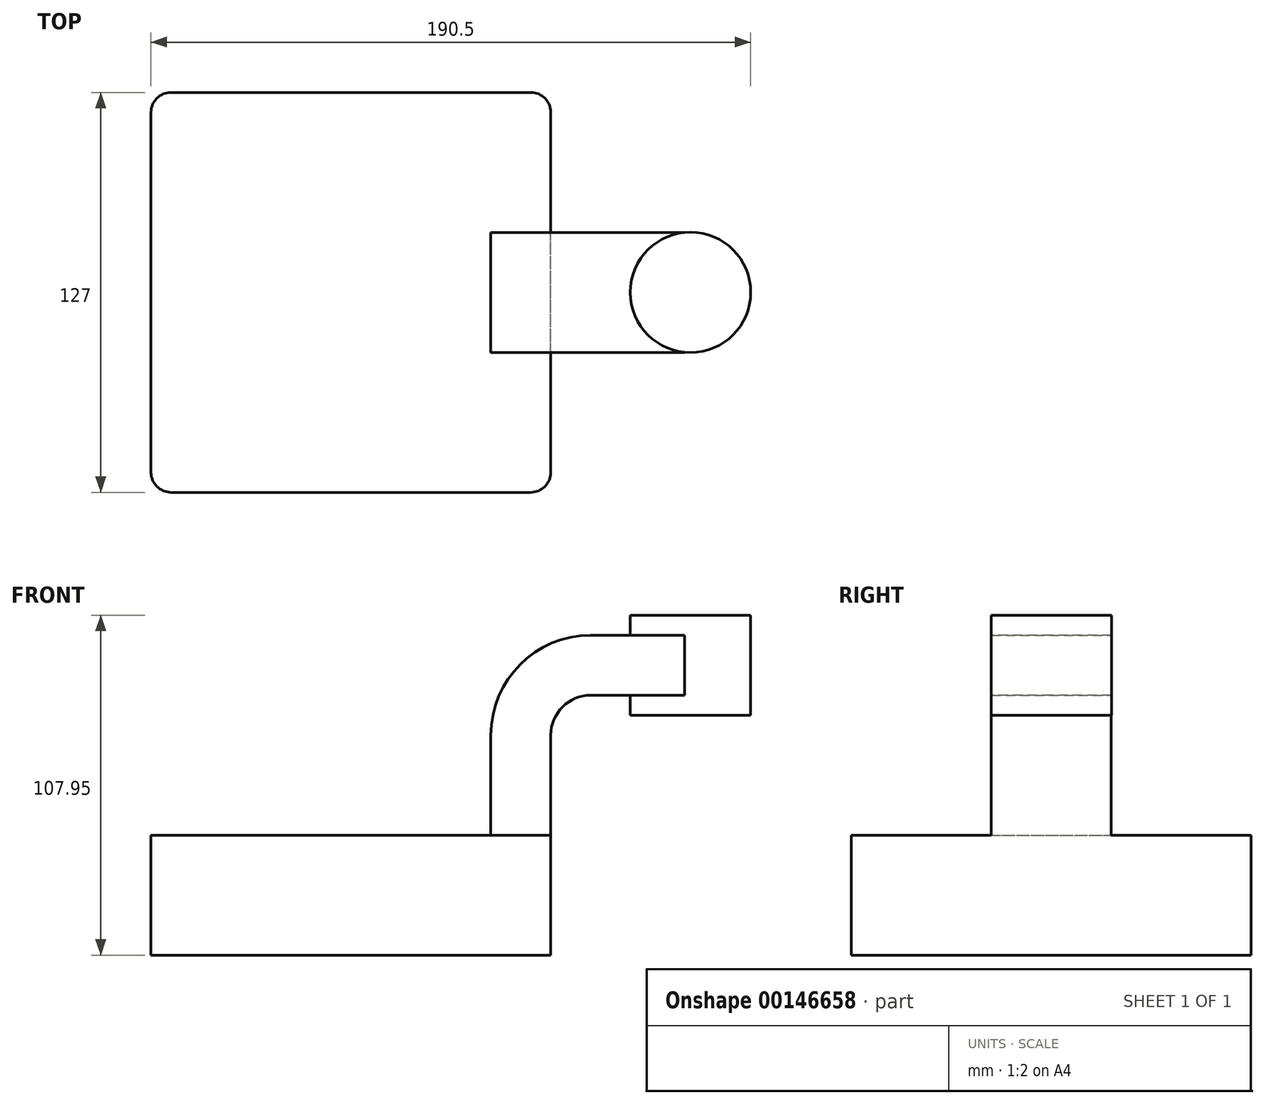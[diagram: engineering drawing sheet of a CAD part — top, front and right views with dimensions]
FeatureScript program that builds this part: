
annotation { "Feature Type Name" : "Feature", "Feature Type Description" : "" }
export const myFeature = defineFeature(function(context is Context, id is Id, definition is map)
    precondition{}
    {
        {
            var Q0;
            Q0=qCreatedBy(makeId("Front.planeOp"),FACE);
            var sketch = newSketch(context, id + "F0", { "sketchPlane" : qUnion([Q0])});
            skLineSegment(sketch, "E0.bottom", {"start": v(63.5, 19.05) * mm, "end": v(-63.5, 19.05) * mm});
            skLineSegment(sketch, "E0.top", {"start": v(63.5, -19.05) * mm, "end": v(-63.5, -19.05) * mm});
            skLineSegment(sketch, "E0.left", {"start": v(63.5, 19.05) * mm, "end": v(63.5, -19.05) * mm});
            skLineSegment(sketch, "E0.right", {"start": v(-63.5, 19.05) * mm, "end": v(-63.5, -19.05) * mm});
            skPoint(sketch, "E0.middle", {"position": v(0, 0) * mm});
            skLineSegment(sketch, "E1.bottom", {"start": v(127, 57.15) * mm, "end": v(88.9, 57.15) * mm});
            skLineSegment(sketch, "E1.top", {"start": v(127, 88.9) * mm, "end": v(88.9, 88.9) * mm});
            skLineSegment(sketch, "E1.left", {"start": v(127, 57.15) * mm, "end": v(127, 88.9) * mm});
            skLineSegment(sketch, "E1.right", {"start": v(88.9, 57.15) * mm, "end": v(88.9, 88.9) * mm});
            skPoint(sketch, "E1.middle", {"position": v(107.95, 73.03) * mm});
            skLineSegment(sketch, "E2", {"start": v(63.5, 19.05) * mm, "end": v(63.5, 50.8) * mm});
            skArc(sketch, "E3", {"start": v(63.5, 50.8) * mm, "mid": v(67.22, 59.78) * mm, "end": v(76.2, 63.5) * mm});
            skLineSegment(sketch, "E4", {"start": v(76.2, 63.5) * mm, "end": v(107.86, 63.5) * mm});
            skLineSegment(sketch, "E5.0", {"start": v(76.2, 82.55) * mm, "end": v(107.86, 82.55) * mm});
            skArc(sketch, "E5.1", {"start": v(44.45, 50.8) * mm, "mid": v(53.75, 73.25) * mm, "end": v(76.2, 82.55) * mm});
            skLineSegment(sketch, "E5.2", {"start": v(44.45, 19.05) * mm, "end": v(44.45, 50.8) * mm});
            skLineSegment(sketch, "E6", {"start": v(107.86, 57.15) * mm, "end": v(107.86, 88.9) * mm});
            skFitSpline(sketch, "E7", {"points": [v(-63.5, 19.05) * mm, v(76.2, 82.55) * mm], "startDerivative": vector(59.97, 153.39) * mm, "endDerivative": vector(184.43, -1.79) * mm});
            skSolve(sketch);
        }
        {
            var Q0;
            Q0=makeQuery(id+"F0.imprint","IMPRINT",FACE,{"disambiguationData":[TD([[makeQuery(id+"F0.imprint","IMPRINT",EDGE,{"derivedFrom":sQuery(id+"F0.wireOp",EDGE,"E0.top")}),-1.0]])]});
            extrude(context, id + "F1", {"entities" : qUnion([Q0]), "endBound" : BoundingType.SYMMETRIC, "depth" : 127 * mm});
        }
        {
            var Q0;
            {var subQ0=sQuery(id+"F0.wireOp",EDGE,"E4");var subQ1=sQuery(id+"F0.wireOp",EDGE,"E1.right");var subQ2=makeQuery(id+"F0.imprint","INTERSECT",VERTEX,{"derivedFrom":[subQ1,subQ0]});Q0=makeQuery(id+"F0.imprint","IMPRINT",FACE,{"disambiguationData":[TD([[makeQuery(id+"F0.imprint","IMPRINT",EDGE,{"disambiguationData":[TD([[subQ2,-1.0]])],"derivedFrom":subQ1}),-1.0]])]});}
            var Q1;
            {var subQ1=sQuery(id+"F0.wireOp",EDGE,"E2");Q1=makeQuery(id+"F0.imprint","IMPRINT",FACE,{"disambiguationData":[TD([[makeQuery(id+"F0.imprint","IMPRINT",EDGE,{"derivedFrom":subQ1}),1.0]])]});}
            extrude(context, id + "F2", {"entities" : qUnion([Q0, Q1]), "operationType" : NewBodyOperationType.ADD, "endBound" : BoundingType.SYMMETRIC, "depth" : 38.1 * mm});
        }
        {
            var Q0;
            Q0=makeQuery(id+"F0.imprint","IMPRINT",FACE,{"disambiguationData":[TD([[makeQuery(id+"F0.imprint","IMPRINT",EDGE,{"derivedFrom":sQuery(id+"F0.wireOp",EDGE,"E5.1")}),1.0]])]});
            extrude(context, id + "F3", {"entities" : qUnion([Q0]), "operationType" : NewBodyOperationType.ADD, "endBound" : BoundingType.SYMMETRIC, "depth" : 15.88 * mm});
        }
        {
            var Q0;
            {var subQ0=sQuery(id+"F0.wireOp",EDGE,"E1.left");Q0=makeQuery(id+"F0.imprint","IMPRINT",FACE,{"disambiguationData":[TD([[makeQuery(id+"F0.imprint","IMPRINT",EDGE,{"derivedFrom":subQ0}),1.0]])]});}
            var Q1;
            Q1=sQuery(id+"F0.wireOp",EDGE,"E6");
            revolve(context, id + "F4", {"operationType" : NewBodyOperationType.ADD, "entities" : qUnion([Q0]), "axis" : qUnion([Q1]), "revolveType" : RevolveType.FULL});
        }
        {
            var Q0;
            Q0=makeQuery(id+"F1.opExtrude","CAP_EDGE",EDGE,{"disambiguationData":[OSD([sQuery(id+"F0.wireOp",EDGE,"E0.right")])],"isStart":true});
            var Q1;
            Q1=makeQuery(id+"F1.opExtrude","CAP_EDGE",EDGE,{"disambiguationData":[OSD([sQuery(id+"F0.wireOp",EDGE,"E0.right")])],"isStart":false});
            var Q2;
            Q2=makeQuery(id+"F1.opExtrude","CAP_EDGE",EDGE,{"disambiguationData":[OSD([sQuery(id+"F0.wireOp",EDGE,"E0.left")])],"isStart":false});
            var Q3;
            Q3=makeQuery(id+"F1.opExtrude","CAP_EDGE",EDGE,{"disambiguationData":[OSD([sQuery(id+"F0.wireOp",EDGE,"E0.left")])],"isStart":true});
            fillet(context, id + "F5", {"entities" : qUnion([Q0, Q1, Q2, Q3]), "radius" : 6.35 * mm, "tangentPropagation" : true, "allowEdgeOverflow" : false});
        }
    });
